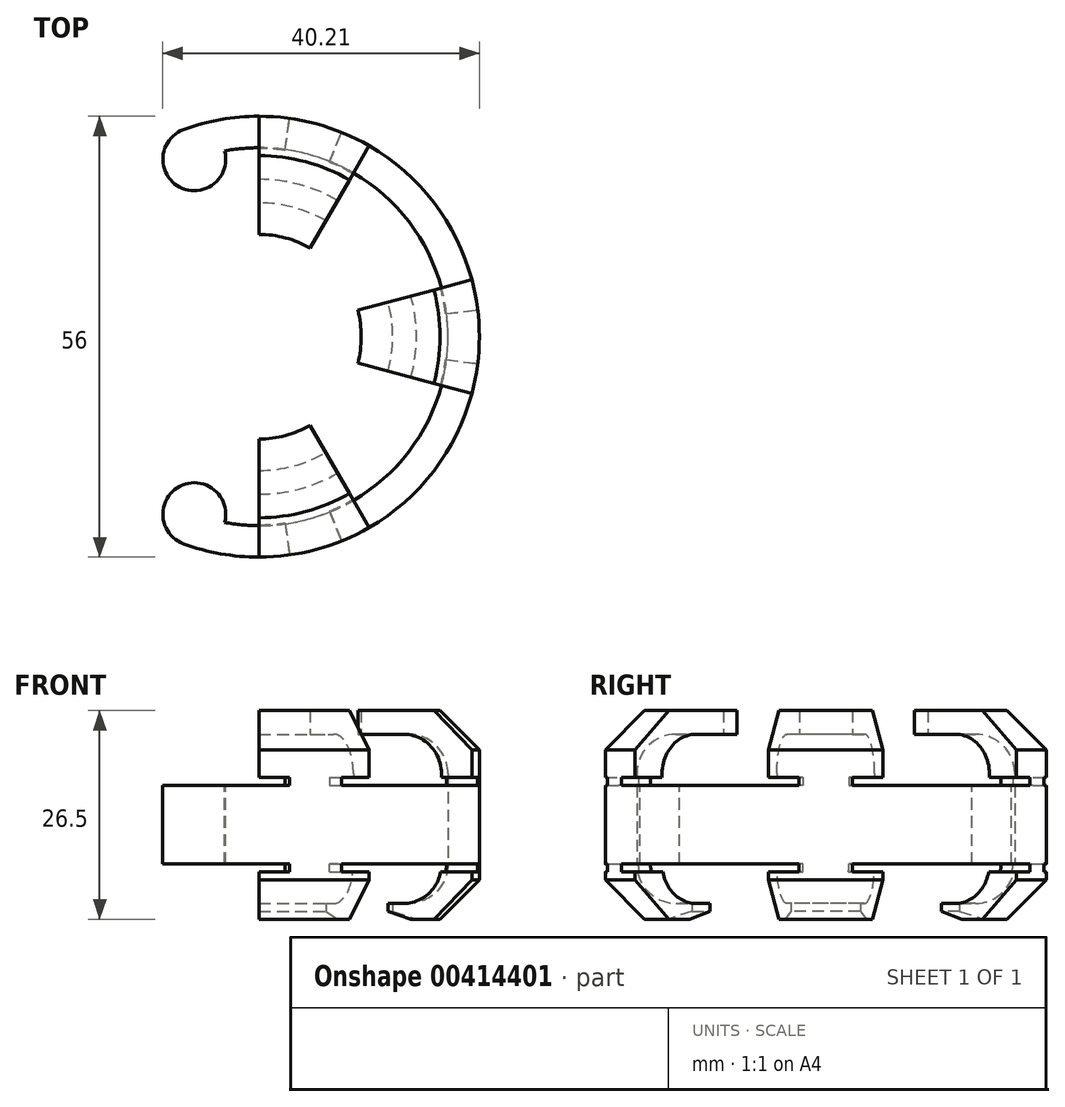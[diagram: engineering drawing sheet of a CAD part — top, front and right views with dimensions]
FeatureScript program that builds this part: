
annotation { "Feature Type Name" : "Feature", "Feature Type Description" : "" }
export const myFeature = defineFeature(function(context is Context, id is Id, definition is map)
    precondition{}
    {
        {
            var Q0;
            Q0=qCreatedBy(makeId("Front.planeOp"),FACE);
            var sketch = newSketch(context, id + "F0", { "sketchPlane" : qUnion([Q0])});
            skLineSegment(sketch, "E0.bottom", {"start": v(0, 0) * mm, "end": v(16, 0) * mm});
            skLineSegment(sketch, "E0.top", {"start": v(0, 20) * mm, "end": v(16, 20) * mm});
            skLineSegment(sketch, "E0.left", {"start": v(0, 0) * mm, "end": v(0, 20) * mm});
            skLineSegment(sketch, "E0.right", {"start": v(22, 6) * mm, "end": v(22, 14) * mm});
            skLineSegment(sketch, "E1.bottom", {"start": v(22, 15) * mm, "end": v(24, 15) * mm});
            skLineSegment(sketch, "E1.top", {"start": v(22, 5) * mm, "end": v(24, 5) * mm});
            skLineSegment(sketch, "E1.left", {"start": v(22, 15) * mm, "end": v(22, 5) * mm});
            skLineSegment(sketch, "E1.right", {"start": v(24, 15) * mm, "end": v(24, 5) * mm});
            skPoint(sketch, "E2.visualSharp", {"position": v(22, 20) * mm});
            skArc(sketch, "E2.filletArc", {"start": v(22, 14) * mm, "mid": v(20.24, 18.24) * mm, "end": v(16, 20) * mm});
            skPoint(sketch, "E3.visualSharp", {"position": v(22, 0) * mm});
            skArc(sketch, "E3.filletArc", {"start": v(16, 0) * mm, "mid": v(20.24, 1.76) * mm, "end": v(22, 6) * mm});
            skLineSegment(sketch, "E4.bottom", {"start": v(24, 15) * mm, "end": v(28, 15) * mm});
            skLineSegment(sketch, "E4.top", {"start": v(24, 5) * mm, "end": v(28, 5) * mm});
            skLineSegment(sketch, "E4.right", {"start": v(28, 15) * mm, "end": v(28, 5) * mm});
            skLineSegment(sketch, "E5", {"start": v(28, 15) * mm, "end": v(28, 24.5) * mm});
            skLineSegment(sketch, "E6", {"start": v(28, 24.5) * mm, "end": v(13, 24.5) * mm});
            skLineSegment(sketch, "E7", {"start": v(13, 24.5) * mm, "end": v(13, 21.5) * mm});
            skLineSegment(sketch, "E8", {"start": v(13, 21.5) * mm, "end": v(24, 21.5) * mm});
            skLineSegment(sketch, "E9", {"start": v(24, 21.5) * mm, "end": v(24, 15) * mm});
            skLineSegment(sketch, "E10", {"start": v(28, 5) * mm, "end": v(28, -2) * mm});
            skLineSegment(sketch, "E11", {"start": v(28, -2) * mm, "end": v(20, -2) * mm});
            skLineSegment(sketch, "E12", {"start": v(17, 0) * mm, "end": v(24, 0) * mm});
            skLineSegment(sketch, "E13", {"start": v(24, 0) * mm, "end": v(24, 5) * mm});
            skLineSegment(sketch, "E14", {"start": v(17, 0) * mm, "end": v(17, -1) * mm});
            skLineSegment(sketch, "E15", {"start": v(17, -1) * mm, "end": v(20, -2) * mm});
            skLineSegment(sketch, "E16", {"start": v(13, 22.5) * mm, "end": v(24, 22.5) * mm, "construction": true});
            skLineSegment(sketch, "E17", {"start": v(24, 22.5) * mm, "end": v(24, 21.5) * mm, "construction": true});
            skSolve(sketch);
        }
        {
            var Q0;
            Q0=makeQuery(id+"F0.imprint","IMPRINT",FACE,{"disambiguationData":[TD([[makeQuery(id+"F0.imprint","IMPRINT",EDGE,{"derivedFrom":sQuery(id+"F0.wireOp",EDGE,"E1.right")}),1.0]])]});
            var Q1;
            Q1=sQuery(id+"F0.wireOp",EDGE,"E0.left");
            revolve(context, id + "F1", {"entities" : qUnion([Q0]), "axis" : qUnion([Q1]), "revolveType" : RevolveType.SYMMETRIC, "angle" : 220 * degree});
        }
        {
            var Q0;
            Q0=makeQuery(id+"F0.imprint","IMPRINT",FACE,{"disambiguationData":[TD([[makeQuery(id+"F0.imprint","IMPRINT",EDGE,{"derivedFrom":sQuery(id+"F0.wireOp",EDGE,"E4.bottom")}),1.0]])]});
            var Q1;
            Q1=makeQuery(id+"F0.imprint","IMPRINT",FACE,{"disambiguationData":[TD([[makeQuery(id+"F0.imprint","IMPRINT",EDGE,{"derivedFrom":sQuery(id+"F0.wireOp",EDGE,"E4.top")}),-1.0]])]});
            var Q2;
            Q2=sQuery(id+"F0.wireOp",EDGE,"E0.left");
            revolve(context, id + "F2", {"operationType" : NewBodyOperationType.ADD, "entities" : qUnion([Q0, Q1]), "axis" : qUnion([Q2]), "revolveType" : RevolveType.TWO_DIRECTIONS, "oppositeDirection" : true, "angle" : 90 * degree, "angleBack" : 60 * degree});
        }
        {
            var Q0;
            Q0=makeQuery(id+"F0.imprint","IMPRINT",FACE,{"disambiguationData":[TD([[makeQuery(id+"F0.imprint","IMPRINT",EDGE,{"derivedFrom":sQuery(id+"F0.wireOp",EDGE,"E4.bottom")}),1.0]])]});
            var Q1;
            Q1=makeQuery(id+"F0.imprint","IMPRINT",FACE,{"disambiguationData":[TD([[makeQuery(id+"F0.imprint","IMPRINT",EDGE,{"derivedFrom":sQuery(id+"F0.wireOp",EDGE,"E4.top")}),-1.0]])]});
            var Q2;
            Q2=sQuery(id+"F0.wireOp",EDGE,"E0.left");
            revolve(context, id + "F3", {"operationType" : NewBodyOperationType.ADD, "entities" : qUnion([Q0, Q1]), "axis" : qUnion([Q2]), "revolveType" : RevolveType.TWO_DIRECTIONS, "angle" : 90 * degree, "angleBack" : 60 * degree});
        }
        {
            var Q0;
            Q0=makeQuery(id+"F0.imprint","IMPRINT",FACE,{"disambiguationData":[TD([[makeQuery(id+"F0.imprint","IMPRINT",EDGE,{"derivedFrom":sQuery(id+"F0.wireOp",EDGE,"E4.bottom")}),1.0]])]});
            var Q1;
            Q1=makeQuery(id+"F0.imprint","IMPRINT",FACE,{"disambiguationData":[TD([[makeQuery(id+"F0.imprint","IMPRINT",EDGE,{"derivedFrom":sQuery(id+"F0.wireOp",EDGE,"E4.top")}),-1.0]])]});
            var Q2;
            Q2=sQuery(id+"F0.wireOp",EDGE,"E0.left");
            revolve(context, id + "F4", {"operationType" : NewBodyOperationType.ADD, "entities" : qUnion([Q0, Q1]), "axis" : qUnion([Q2]), "revolveType" : RevolveType.SYMMETRIC, "angle" : 30 * degree});
        }
        {
            var Q0;
            {var subQ3=sQuery(id+"F0.wireOp",EDGE,"E1.right");var subQ11=sQuery(id+"F0.wireOp",EDGE,"E4.bottom");var subQ13=sQuery(id+"F0.wireOp",EDGE,"E4.right");var subQ15=makeQuery(id+"F1.opRevolve","CAP_FACE",FACE,{"disambiguationData":[OSD([subQ3,subQ11,sQuery(id+"F0.wireOp",EDGE,"E4.top"),subQ13])],"isStart":false});Q0=makeQuery(id+"F3.boolean.opBoolean","SPLIT",FACE,{"disambiguationData":[TD([subQ15])],"derivedFrom":makeQuery(id+"F2.boolean.opBoolean","SPLIT",FACE,{"disambiguationData":[TD([subQ15])],"derivedFrom":makeQuery(id+"F1.opRevolve","SWEPT_FACE",FACE,{"disambiguationData":[OSD([subQ11])]})})});}
            var sketch = newSketch(context, id + "F5", { "sketchPlane" : qUnion([Q0])});
            skCircle(sketch, "E18", {"center": v(-8.2, 22.55) * mm, "radius": 4 * mm});
            skLineSegment(sketch, "E19", {"start": v(-11, 0) * mm, "end": v(11, 0) * mm, "construction": true});
            skCircle(sketch, "E20.MirrorC", {"center": v(-8.2, -22.55) * mm, "radius": 4 * mm});
            skSolve(sketch);
        }
        {
            var Q0;
            Q0 = qSketchRegion(id + "F5", true);
            var Q1;
            {var subQ2=sQuery(id+"F0.wireOp",EDGE,"E4.top");var subQ3=sQuery(id+"F0.wireOp",EDGE,"E4.right");var subQ4=sQuery(id+"F0.wireOp",EDGE,"E1.right");Q1=makeQuery(id+"F2.boolean.opBoolean","SPLIT",FACE,{"disambiguationData":[TD([makeQuery(id+"F1.opRevolve","CAP_FACE",FACE,{"disambiguationData":[OSD([subQ4,sQuery(id+"F0.wireOp",EDGE,"E4.bottom"),subQ2,subQ3])],"isStart":true})])],"derivedFrom":makeQuery(id+"F1.opRevolve","SWEPT_FACE",FACE,{"disambiguationData":[OSD([subQ2])]})});}
            extrude(context, id + "F6", {"entities" : qUnion([Q0]), "operationType" : NewBodyOperationType.ADD, "endBound" : BoundingType.UP_TO_SURFACE, "oppositeDirection" : true, "endBoundEntityFace" : qUnion([Q1]), "depth" : 25 * mm});
        }
        {
            var Q0;
            Q0=makeQuery(id+"F4.opRevolve","SWEPT_EDGE",EDGE,{"disambiguationData":[OSD([sQuery(id+"F0.wireOp",EDGE,"E8"),sQuery(id+"F0.wireOp",EDGE,"E9")])]});
            var Q1;
            Q1=makeQuery(id+"F3.opRevolve","SWEPT_EDGE",EDGE,{"disambiguationData":[OSD([sQuery(id+"F0.wireOp",EDGE,"E8"),sQuery(id+"F0.wireOp",EDGE,"E9")])]});
            var Q2;
            Q2=makeQuery(id+"F2.opRevolve","SWEPT_EDGE",EDGE,{"disambiguationData":[OSD([sQuery(id+"F0.wireOp",EDGE,"E8"),sQuery(id+"F0.wireOp",EDGE,"E9")])]});
            var Q3;
            Q3=makeQuery(id+"F2.opRevolve","SWEPT_EDGE",EDGE,{"disambiguationData":[OSD([sQuery(id+"F0.wireOp",EDGE,"E12"),sQuery(id+"F0.wireOp",EDGE,"E13")])]});
            var Q4;
            Q4=makeQuery(id+"F3.opRevolve","SWEPT_EDGE",EDGE,{"disambiguationData":[OSD([sQuery(id+"F0.wireOp",EDGE,"E12"),sQuery(id+"F0.wireOp",EDGE,"E13")])]});
            var Q5;
            Q5=makeQuery(id+"F4.opRevolve","SWEPT_EDGE",EDGE,{"disambiguationData":[OSD([sQuery(id+"F0.wireOp",EDGE,"E12"),sQuery(id+"F0.wireOp",EDGE,"E13")])]});
            fillet(context, id + "F7", {"entities" : qUnion([Q0, Q1, Q2, Q3, Q4, Q5]), "radius" : 5 * mm, "tangentPropagation" : true, "allowEdgeOverflow" : false});
        }
        {
            var Q0;
            Q0=makeQuery(id+"F3.opRevolve","SWEPT_EDGE",EDGE,{"disambiguationData":[OSD([sQuery(id+"F0.wireOp",EDGE,"E5"),sQuery(id+"F0.wireOp",EDGE,"E6")])]});
            var Q1;
            Q1=makeQuery(id+"F4.opRevolve","SWEPT_EDGE",EDGE,{"disambiguationData":[OSD([sQuery(id+"F0.wireOp",EDGE,"E5"),sQuery(id+"F0.wireOp",EDGE,"E6")])]});
            var Q2;
            Q2=makeQuery(id+"F2.opRevolve","SWEPT_EDGE",EDGE,{"disambiguationData":[OSD([sQuery(id+"F0.wireOp",EDGE,"E5"),sQuery(id+"F0.wireOp",EDGE,"E6")])]});
            var Q3;
            Q3=makeQuery(id+"F2.opRevolve","SWEPT_EDGE",EDGE,{"disambiguationData":[OSD([sQuery(id+"F0.wireOp",EDGE,"E10"),sQuery(id+"F0.wireOp",EDGE,"E11")])]});
            var Q4;
            Q4=makeQuery(id+"F3.opRevolve","SWEPT_EDGE",EDGE,{"disambiguationData":[OSD([sQuery(id+"F0.wireOp",EDGE,"E10"),sQuery(id+"F0.wireOp",EDGE,"E11")])]});
            var Q5;
            Q5=makeQuery(id+"F4.opRevolve","SWEPT_EDGE",EDGE,{"disambiguationData":[OSD([sQuery(id+"F0.wireOp",EDGE,"E10"),sQuery(id+"F0.wireOp",EDGE,"E11")])]});
            chamfer(context, id + "F8", {"entities" : qUnion([Q0, Q1, Q2, Q3, Q4, Q5]), "width" : 5 * mm, "tangentPropagation" : true});
        }
        {
            var Q0;
            Q0=qCreatedBy(makeId("Front.planeOp"),FACE);
            var sketch = newSketch(context, id + "F9", { "sketchPlane" : qUnion([Q0])});
            skLineSegment(sketch, "E21.bottom", {"start": v(22, 16) * mm, "end": v(32, 16) * mm});
            skLineSegment(sketch, "E21.top", {"start": v(22, 15) * mm, "end": v(32, 15) * mm});
            skLineSegment(sketch, "E21.left", {"start": v(22, 16) * mm, "end": v(22, 15) * mm});
            skLineSegment(sketch, "E21.right", {"start": v(32, 16) * mm, "end": v(32, 15) * mm});
            skLineSegment(sketch, "E22.bottom", {"start": v(22, 5) * mm, "end": v(32, 5) * mm});
            skLineSegment(sketch, "E22.top", {"start": v(22, 4) * mm, "end": v(32, 4) * mm});
            skLineSegment(sketch, "E22.left", {"start": v(22, 5) * mm, "end": v(22, 4) * mm});
            skLineSegment(sketch, "E22.right", {"start": v(32, 5) * mm, "end": v(32, 4) * mm});
            skSolve(sketch);
        }
        {
            var Q0;
            Q0 = qSketchRegion(id + "F9", true);
            var Q1;
            Q1=sQuery(id+"F0.wireOp",EDGE,"E0.left");
            revolve(context, id + "F10", {"operationType" : NewBodyOperationType.REMOVE, "entities" : qUnion([Q0]), "axis" : qUnion([Q1]), "revolveType" : RevolveType.TWO_DIRECTIONS, "oppositeDirection" : true, "angle" : 20 * degree, "angleBack" : 7 * degree});
        }
        {
            var Q0;
            Q0 = qSketchRegion(id + "F9", true);
            var Q1;
            Q1=sQuery(id+"F0.wireOp",EDGE,"E0.left");
            revolve(context, id + "F11", {"operationType" : NewBodyOperationType.REMOVE, "entities" : qUnion([Q0]), "axis" : qUnion([Q1]), "revolveType" : RevolveType.TWO_DIRECTIONS, "angle" : 20 * degree, "angleBack" : 7 * degree});
        }
        {
            var Q0;
            Q0 = qSketchRegion(id + "F9", true);
            var Q1;
            Q1=sQuery(id+"F0.wireOp",EDGE,"E0.left");
            revolve(context, id + "F12", {"operationType" : NewBodyOperationType.REMOVE, "entities" : qUnion([Q0]), "axis" : qUnion([Q1]), "revolveType" : RevolveType.TWO_DIRECTIONS, "angle" : 95 * degree, "angleBack" : 82 * degree});
        }
        {
            var Q0;
            Q0 = qSketchRegion(id + "F9", true);
            var Q1;
            Q1=sQuery(id+"F0.wireOp",EDGE,"E0.left");
            revolve(context, id + "F13", {"operationType" : NewBodyOperationType.REMOVE, "entities" : qUnion([Q0]), "axis" : qUnion([Q1]), "revolveType" : RevolveType.TWO_DIRECTIONS, "oppositeDirection" : true, "angle" : 95 * degree, "angleBack" : 82 * degree});
        }
        {
            var Q0;
            Q0 = qSketchRegion(id + "F9", true);
            var Q1;
            Q1=sQuery(id+"F0.wireOp",EDGE,"E0.left");
            revolve(context, id + "F14", {"operationType" : NewBodyOperationType.REMOVE, "entities" : qUnion([Q0]), "axis" : qUnion([Q1]), "revolveType" : RevolveType.TWO_DIRECTIONS, "oppositeDirection" : true, "angle" : 68 * degree, "angleBack" : 55 * degree});
        }
        {
            var Q0;
            Q0 = qSketchRegion(id + "F9", true);
            var Q1;
            Q1=sQuery(id+"F0.wireOp",EDGE,"E0.left");
            revolve(context, id + "F15", {"operationType" : NewBodyOperationType.REMOVE, "entities" : qUnion([Q0]), "axis" : qUnion([Q1]), "revolveType" : RevolveType.TWO_DIRECTIONS, "angle" : 68 * degree, "angleBack" : 55 * degree});
        }
    });
